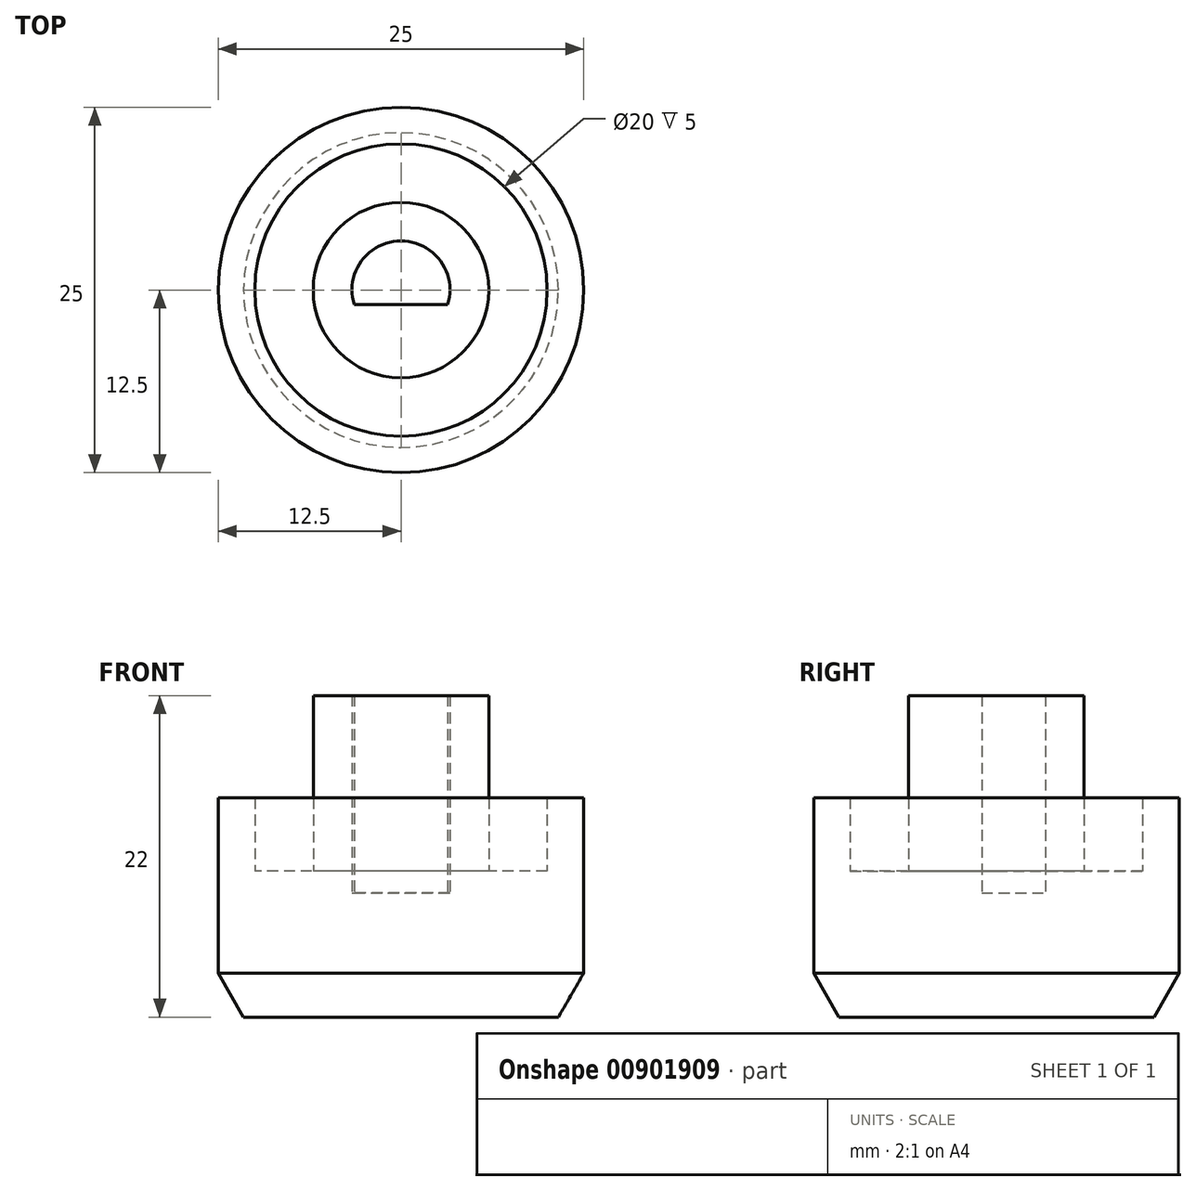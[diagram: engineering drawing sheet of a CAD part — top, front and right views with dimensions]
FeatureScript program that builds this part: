
annotation { "Feature Type Name" : "Feature", "Feature Type Description" : "" }
export const myFeature = defineFeature(function(context is Context, id is Id, definition is map)
    precondition{}
    {
        {
            var Q0;
            Q0=qCreatedBy(makeId("Top.planeOp"),FACE);
            var sketch = newSketch(context, id + "F0", { "sketchPlane" : qUnion([Q0])});
            skCircle(sketch, "E0", {"center": v(0, 0) * mm, "radius": 12.5 * mm});
            skCircle(sketch, "E1", {"center": v(0, 0) * mm, "radius": 6 * mm});
            skArc(sketch, "E2", {"start": v(3.2, -1) * mm, "mid": v(0, 3.35) * mm, "end": v(-3.2, -1) * mm});
            skLineSegment(sketch, "E3", {"start": v(-3.2, -1) * mm, "end": v(3.2, -1) * mm});
            skLineSegment(sketch, "E4", {"start": v(0, 3.35) * mm, "end": v(2.85, 3.35) * mm, "construction": true});
            skCircle(sketch, "E5", {"center": v(0, 0) * mm, "radius": 10 * mm});
            skSolve(sketch);
        }
        {
            var Q0;
            Q0=makeQuery(id+"F0.imprint","IMPRINT",FACE,{"disambiguationData":[TD([[makeQuery(id+"F0.imprint","IMPRINT",EDGE,{"derivedFrom":sQuery(id+"F0.wireOp",EDGE,"E0")}),1.0]])]});
            extrude(context, id + "F1", {"entities" : qUnion([Q0]), "depth" : 15 * mm, "offsetDistance" : 25 * mm});
        }
        {
            var Q0;
            Q0=makeQuery(id+"F0.imprint","IMPRINT",FACE,{"disambiguationData":[TD([[makeQuery(id+"F0.imprint","IMPRINT",EDGE,{"derivedFrom":sQuery(id+"F0.wireOp",EDGE,"E1")}),-1.0]])]});
            extrude(context, id + "F2", {"entities" : qUnion([Q0]), "operationType" : NewBodyOperationType.ADD, "depth" : 10 * mm, "offsetDistance" : 25 * mm});
        }
        {
            var Q0;
            Q0=makeQuery(id+"F0.imprint","IMPRINT",FACE,{"disambiguationData":[TD([[makeQuery(id+"F0.imprint","IMPRINT",EDGE,{"derivedFrom":sQuery(id+"F0.wireOp",EDGE,"E1")}),1.0]])]});
            extrude(context, id + "F3", {"entities" : qUnion([Q0]), "operationType" : NewBodyOperationType.ADD, "depth" : 22 * mm, "offsetDistance" : 25 * mm});
        }
        {
            var Q0;
            Q0=makeQuery(id+"F0.imprint","IMPRINT",FACE,{"disambiguationData":[TD([[makeQuery(id+"F0.imprint","IMPRINT",EDGE,{"derivedFrom":sQuery(id+"F0.wireOp",EDGE,"E2")}),1.0]])]});
            extrude(context, id + "F4", {"entities" : qUnion([Q0]), "operationType" : NewBodyOperationType.ADD, "depth" : 8.5 * mm, "offsetDistance" : 25 * mm});
        }
        {
            var Q0;
            Q0=makeQuery(id+"F1.opExtrude","CAP_EDGE",EDGE,{"disambiguationData":[OSD([sQuery(id+"F0.wireOp",EDGE,"E0")])],"isStart":true});
            chamfer(context, id + "F5", {"entities" : qUnion([Q0]), "chamferType" : ChamferType.OFFSET_ANGLE, "width" : 3 * mm, "oppositeDirection" : false, "angle" : 30 * degree, "tangentPropagation" : true});
        }
    });
